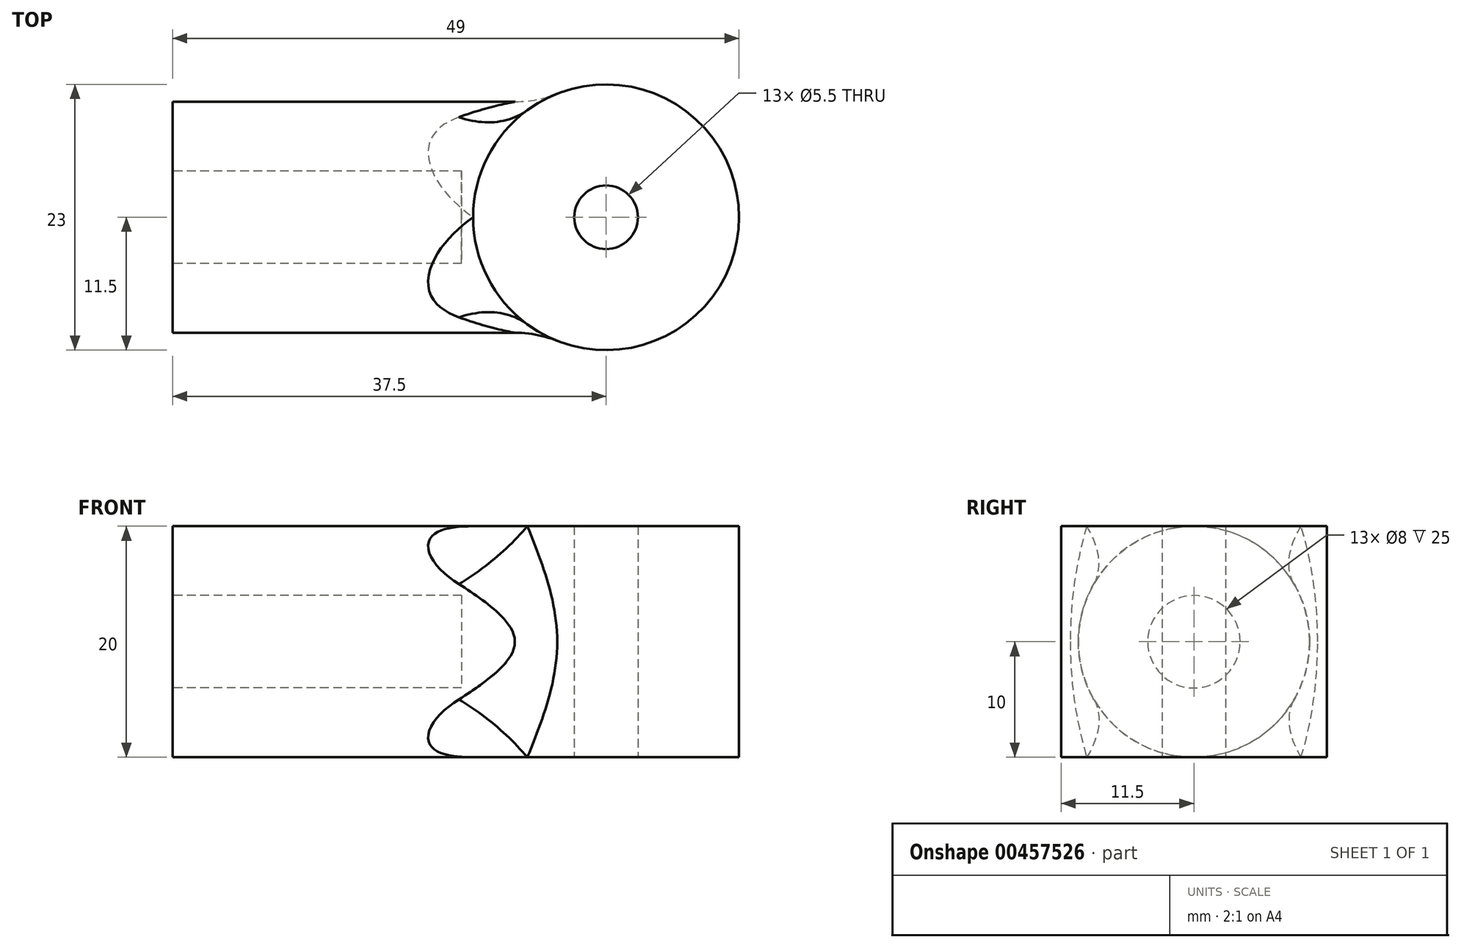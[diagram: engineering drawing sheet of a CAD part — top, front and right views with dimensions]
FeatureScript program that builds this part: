
annotation { "Feature Type Name" : "Feature", "Feature Type Description" : "" }
export const myFeature = defineFeature(function(context is Context, id is Id, definition is map)
    precondition{}
    {
        {
            var Q0;
            Q0=qCreatedBy(makeId("Top.planeOp"),FACE);
            var sketch = newSketch(context, id + "F0", { "sketchPlane" : qUnion([Q0])});
            skCircle(sketch, "E0", {"center": v(0, 0) * mm, "radius": 11.5 * mm});
            skCircle(sketch, "E1", {"center": v(0, 0) * mm, "radius": 17.5 * mm});
            skLineSegment(sketch, "E2.bottom", {"start": v(-37.5, -10) * mm, "end": v(37.5, -10) * mm});
            skLineSegment(sketch, "E2.top", {"start": v(-37.5, 10) * mm, "end": v(37.5, 10) * mm});
            skLineSegment(sketch, "E2.left", {"start": v(-37.5, -10) * mm, "end": v(-37.5, 10) * mm});
            skLineSegment(sketch, "E2.right", {"start": v(37.5, -10) * mm, "end": v(37.5, 10) * mm});
            skLineSegment(sketch, "E3", {"start": v(0, 10) * mm, "end": v(0, -10) * mm});
            skCircle(sketch, "E4", {"center": v(0, 0) * mm, "radius": 2.75 * mm});
            skSolve(sketch);
        }
        {
            var Q0;
            {var subQ5=sQuery(id+"F0.wireOp",EDGE,"E2.left");Q0=makeQuery(id+"F0.imprint","IMPRINT",FACE,{"disambiguationData":[TD([[makeQuery(id+"F0.imprint","IMPRINT",EDGE,{"derivedFrom":subQ5}),-1.0]])]});}
            var Q1;
            {var subQ0=sQuery(id+"F0.wireOp",EDGE,"E2.top");var subQ1=sQuery(id+"F0.wireOp",EDGE,"E0");var subQ2=makeQuery(id+"F0.imprint","INTERSECT",VERTEX,{"disambiguationData":[OD(0.0)],"derivedFrom":[subQ1,subQ0]});Q1=makeQuery(id+"F0.imprint","IMPRINT",FACE,{"disambiguationData":[TD([[makeQuery(id+"F0.imprint","IMPRINT",EDGE,{"disambiguationData":[TD([[subQ2,-1.0]])],"derivedFrom":subQ1}),-1.0]])]});}
            var Q2;
            {var subQ5=sQuery(id+"F0.wireOp",EDGE,"E3");Q2=makeQuery(id+"F0.imprint","IMPRINT",FACE,{"disambiguationData":[TD([[makeQuery(id+"F0.imprint","IMPRINT",EDGE,{"derivedFrom":subQ5}),-1.0]])]});}
            var Q3;
            {var subQ0=sQuery(id+"F0.wireOp",EDGE,"E2.bottom");var subQ1=sQuery(id+"F0.wireOp",EDGE,"E0");var subQ2=makeQuery(id+"F0.imprint","INTERSECT",VERTEX,{"disambiguationData":[OD(0.0)],"derivedFrom":[subQ1,subQ0]});Q3=makeQuery(id+"F0.imprint","IMPRINT",FACE,{"disambiguationData":[TD([[makeQuery(id+"F0.imprint","IMPRINT",EDGE,{"disambiguationData":[TD([[subQ2,-1.0]])],"derivedFrom":subQ1}),1.0]])]});}
            var Q4;
            {var subQ5=sQuery(id+"F0.wireOp",EDGE,"E3");Q4=makeQuery(id+"F0.imprint","IMPRINT",FACE,{"disambiguationData":[TD([[makeQuery(id+"F0.imprint","IMPRINT",EDGE,{"derivedFrom":subQ5}),1.0]])]});}
            var Q5;
            {var subQ0=sQuery(id+"F0.wireOp",EDGE,"E2.top");var subQ1=sQuery(id+"F0.wireOp",EDGE,"E0");var subQ2=makeQuery(id+"F0.imprint","INTERSECT",VERTEX,{"disambiguationData":[OD(0.0)],"derivedFrom":[subQ1,subQ0]});Q5=makeQuery(id+"F0.imprint","IMPRINT",FACE,{"disambiguationData":[TD([[makeQuery(id+"F0.imprint","IMPRINT",EDGE,{"disambiguationData":[TD([[subQ2,1.0]])],"derivedFrom":subQ1}),1.0]])]});}
            extrude(context, id + "F1", {"entities" : qUnion([Q0, Q1, Q2, Q3, Q4, Q5]), "depth" : 20 * mm});
        }
        {
            var Q0;
            Q0=makeQuery(id+"F1.opExtrude","CAP_EDGE",EDGE,{"disambiguationData":[OSD([sQuery(id+"F0.wireOp",EDGE,"E2.top")])],"isStart":false});
            var Q1;
            Q1=makeQuery(id+"F1.opExtrude","CAP_EDGE",EDGE,{"disambiguationData":[OSD([sQuery(id+"F0.wireOp",EDGE,"E2.bottom")])],"isStart":false});
            var Q2;
            Q2=makeQuery(id+"F1.opExtrude","CAP_EDGE",EDGE,{"disambiguationData":[OSD([sQuery(id+"F0.wireOp",EDGE,"E2.top")])],"isStart":true});
            var Q3;
            Q3=makeQuery(id+"F1.opExtrude","CAP_EDGE",EDGE,{"disambiguationData":[OSD([sQuery(id+"F0.wireOp",EDGE,"E2.bottom")])],"isStart":true});
            fillet(context, id + "F2", {"entities" : qUnion([Q0, Q1, Q2, Q3]), "radius" : 10 * mm, "tangentPropagation" : true, "allowEdgeOverflow" : false});
        }
        {
            var Q0;
            Q0=makeQuery(id+"F1.opExtrude","SWEPT_FACE",FACE,{"disambiguationData":[OSD([sQuery(id+"F0.wireOp",EDGE,"E2.left")])]});
            cPlane(context, id + "F3", {"entities" : qUnion([Q0]), "cplaneType" : CPlaneType.OFFSET, "offset" : 0 * mm, "width" : 150 * mm, "height" : 150 * mm});
        }
        {
            var Q0;
            Q0=qCreatedBy(id+"F3.planeOp",FACE);
            var sketch = newSketch(context, id + "F4", { "sketchPlane" : qUnion([Q0])});
            skLineSegment(sketch, "E5", {"start": v(0, 0) * mm, "end": v(0, 10) * mm, "construction": true});
            skCircle(sketch, "E6", {"center": v(0, 10) * mm, "radius": 4 * mm});
            skSolve(sketch);
        }
        {
            var Q0;
            Q0=qSketchRegion(id+"F4",true);
            extrude(context, id + "F5", {"entities" : qUnion([Q0]), "operationType" : NewBodyOperationType.REMOVE, "oppositeDirection" : true, "depth" : 25 * mm});
        }
        {
            var Q0;
            Q0=makeQuery(id+"F2.opFillet","BLEND_EDGE",EDGE,{"blendedFrom":[makeQuery(id+"F1.opExtrude","CAP_EDGE",EDGE,{"disambiguationData":[OSD([sQuery(id+"F0.wireOp",EDGE,"E2.bottom")])],"isStart":false}),makeQuery(id+"F1.opExtrude","SWEPT_FACE",FACE,{"disambiguationData":[OSD([sQuery(id+"F0.wireOp",EDGE,"E0")])]})],"blendedInto":[makeQuery(id+"F1.opExtrude","SWEPT_FACE",FACE,{"disambiguationData":[OSD([sQuery(id+"F0.wireOp",EDGE,"E0")])]})]});
            fillet(context, id + "F6", {"entities" : qUnion([Q0]), "radius" : 10 * mm, "tangentPropagation" : true, "allowEdgeOverflow" : false});
        }
    });
